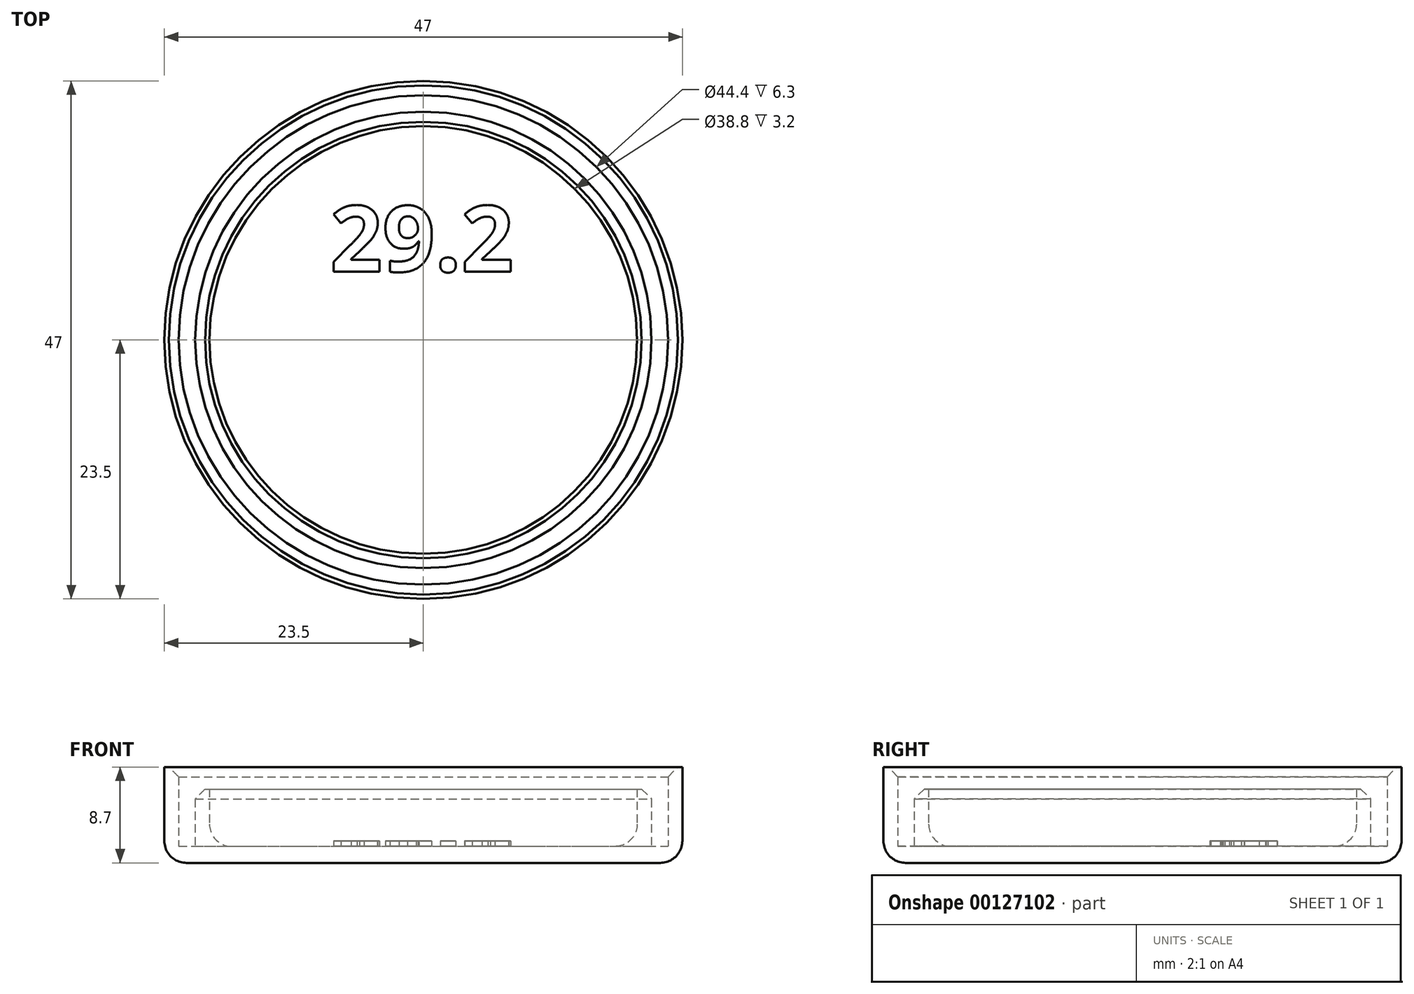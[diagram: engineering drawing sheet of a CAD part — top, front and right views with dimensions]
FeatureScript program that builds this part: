
annotation { "Feature Type Name" : "Feature", "Feature Type Description" : "" }
export const myFeature = defineFeature(function(context is Context, id is Id, definition is map)
    precondition{}
    {
        {
            var Q0;
            Q0=qCreatedBy(makeId("Front.planeOp"),FACE);
            var sketch = newSketch(context, id + "F0", { "sketchPlane" : qUnion([Q0])});
            skLineSegment(sketch, "E0", {"start": v(0, 0) * mm, "end": v(21.5, 0) * mm});
            skLineSegment(sketch, "E1", {"start": v(0, 0) * mm, "end": v(0, 1.5) * mm});
            skLineSegment(sketch, "E2", {"start": v(0, 1.5) * mm, "end": v(17.4, 1.5) * mm});
            skLineSegment(sketch, "E3", {"start": v(19.4, 3.5) * mm, "end": v(19.4, 6.7) * mm});
            skLineSegment(sketch, "E4", {"start": v(19.4, 6.7) * mm, "end": v(19.8, 6.7) * mm});
            skLineSegment(sketch, "E5", {"start": v(19.8, 6.7) * mm, "end": v(20.7, 5.8) * mm});
            skLineSegment(sketch, "E6", {"start": v(20.7, 5.8) * mm, "end": v(20.7, 1.5) * mm});
            skLineSegment(sketch, "E7", {"start": v(20.7, 1.5) * mm, "end": v(22.2, 1.5) * mm});
            skLineSegment(sketch, "E8", {"start": v(22.2, 1.5) * mm, "end": v(22.2, 7.8) * mm});
            skLineSegment(sketch, "E9", {"start": v(22.2, 7.8) * mm, "end": v(23.1, 8.7) * mm});
            skLineSegment(sketch, "E10", {"start": v(23.1, 8.7) * mm, "end": v(23.5, 8.7) * mm});
            skLineSegment(sketch, "E11", {"start": v(23.5, 8.7) * mm, "end": v(23.5, 2) * mm});
            skArc(sketch, "E12", {"start": v(17.4, 1.5) * mm, "mid": v(18.81, 2.09) * mm, "end": v(19.4, 3.5) * mm});
            skArc(sketch, "E13", {"start": v(21.5, 0) * mm, "mid": v(22.91, 0.59) * mm, "end": v(23.5, 2) * mm});
            skSolve(sketch);
        }
        {
            var Q0;
            Q0 = qSketchRegion(id + "F0", true);
            var Q1;
            Q1=sQuery(id+"F0.wireOp",EDGE,"E1");
            revolve(context, id + "F1", {"entities" : qUnion([Q0]), "axis" : qUnion([Q1]), "revolveType" : RevolveType.FULL});
        }
        {
            var Q0;
            Q0=makeQuery(id+"F1.opRevolve","SWEPT_FACE",FACE,{"disambiguationData":[OSD([sQuery(id+"F0.wireOp",EDGE,"E2")])]});
            var sketch = newSketch(context, id + "F2", { "sketchPlane" : qUnion([Q0])});
            skText(sketch, "E14", { "text": "29.2", "fontName": "OpenSans-Bold.ttf"});
            const initialGuessF2  = {"E14": [-0.00846, 0.00621, 1, 0, 0.006]};
            skSetInitialGuess(sketch, initialGuessF2);
            skSolve(sketch);
        }
        {
            var Q0;
            Q0 = qSketchRegion(id + "F2", true);
            extrude(context, id + "F3", {"entities" : qUnion([Q0]), "operationType" : NewBodyOperationType.ADD, "depth" : 0.5 * mm});
        }
    });
